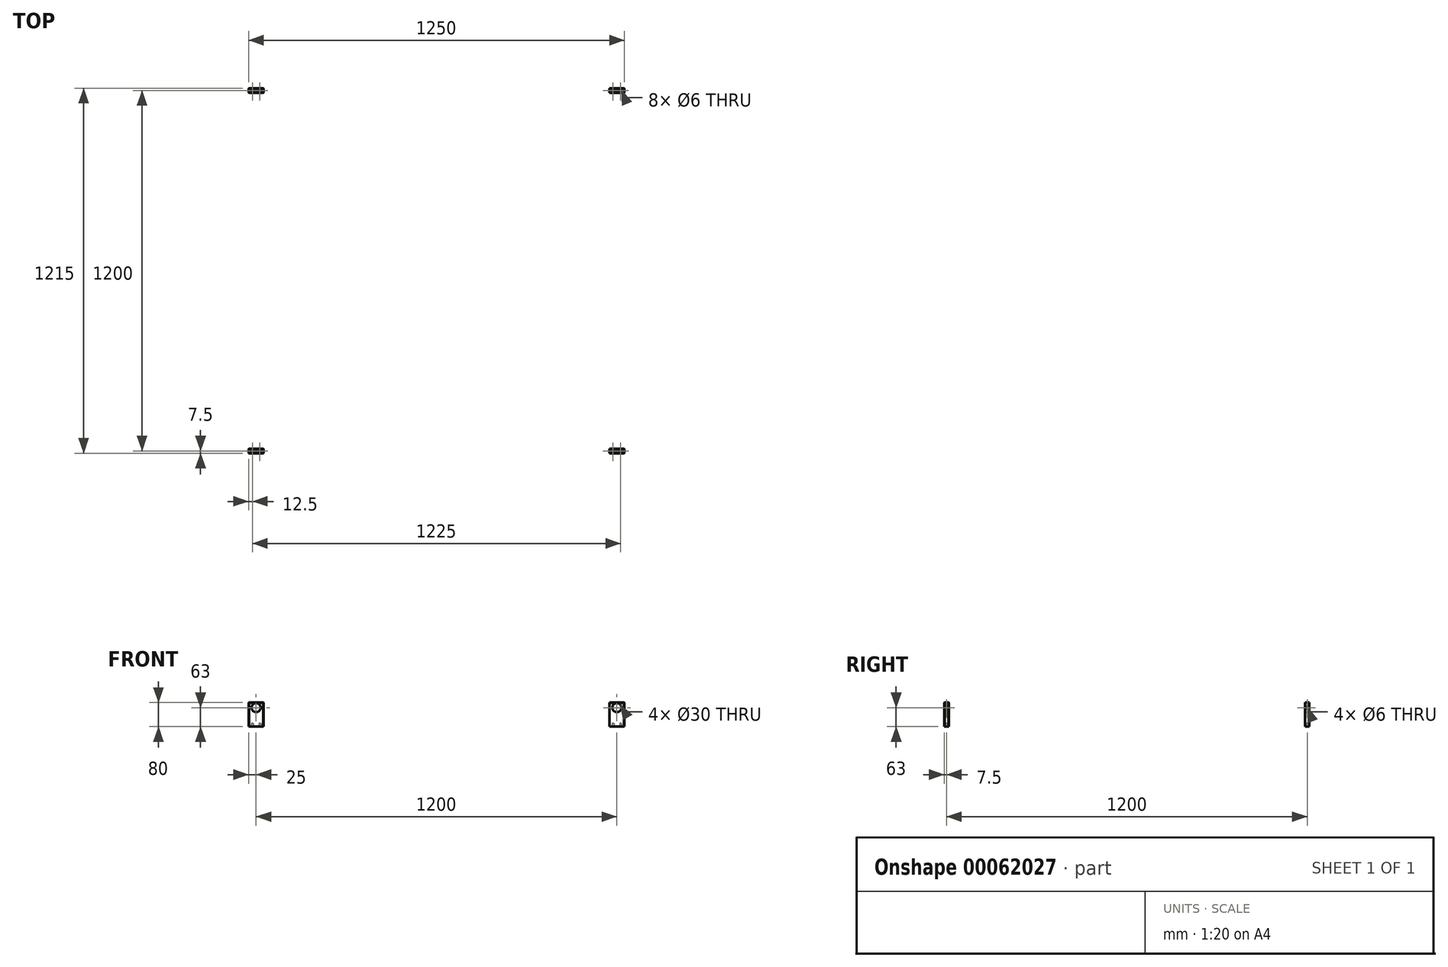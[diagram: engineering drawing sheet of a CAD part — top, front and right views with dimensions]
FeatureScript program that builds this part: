
annotation { "Feature Type Name" : "Feature", "Feature Type Description" : "" }
export const myFeature = defineFeature(function(context is Context, id is Id, definition is map)
    precondition{}
    {
        {
            var Q0;
            Q0=qCreatedBy(makeId("Front.planeOp"),FACE);
            var sketch = newSketch(context, id + "F0", { "sketchPlane" : qUnion([Q0])});
            skCircle(sketch, "E0", {"center": v(0, 0) * mm, "radius": 15 * mm});
            skLineSegment(sketch, "E1.bottom", {"start": v(-25, 17) * mm, "end": v(25, 17) * mm});
            skLineSegment(sketch, "E1.top", {"start": v(-25, -63) * mm, "end": v(25, -63) * mm});
            skLineSegment(sketch, "E1.left", {"start": v(-25, 17) * mm, "end": v(-25, -63) * mm});
            skLineSegment(sketch, "E1.right", {"start": v(25, 17) * mm, "end": v(25, -63) * mm});
            skSolve(sketch);
        }
        {
            var Q0;
            Q0=makeQuery(id+"F0.imprint","IMPRINT",FACE,{"disambiguationData":[TD([[makeQuery(id+"F0.imprint","IMPRINT",EDGE,{"derivedFrom":sQuery(id+"F0.wireOp",EDGE,"E0")}),-1.0]])]});
            extrude(context, id + "F1", {"entities" : qUnion([Q0]), "depth" : 15 * mm});
        }
        {
            var Q0;
            Q0=makeQuery(id+"F1.opExtrude","SWEPT_FACE",FACE,{"disambiguationData":[OSD([sQuery(id+"F0.wireOp",EDGE,"E1.top")])]});
            var sketch = newSketch(context, id + "F2", { "sketchPlane" : qUnion([Q0])});
            skCircle(sketch, "E2", {"center": v(12.5, 7.5) * mm, "radius": 3 * mm});
            skCircle(sketch, "E3.MirrorC", {"center": v(-12.5, 7.5) * mm, "radius": 3 * mm});
            skSolve(sketch);
        }
        {
            var Q0;
            Q0=sQuery(id+"F2.wireOp",VERTEX,"E2.center");
            var Q1;
            Q1=sQuery(id+"F2.wireOp",VERTEX,"E3.MirrorC.center");
            var Q2;
            Q2=makeQuery(id+"F1.opExtrude","SWEPT_BODY",BODY,{"disambiguationData":[OSD([sQuery(id+"F0.wireOp",EDGE,"E0"),sQuery(id+"F0.wireOp",EDGE,"E1.bottom"),sQuery(id+"F0.wireOp",EDGE,"E1.top"),sQuery(id+"F0.wireOp",EDGE,"E1.left"),sQuery(id+"F0.wireOp",EDGE,"E1.right")])]});
            hole(context, id + "F3", {"style" : HoleStyle.SIMPLE, "holeDiameter" : 6 * mm, "endStyle" : HoleEndStyle.BLIND, "holeDepth" : 10 * mm, "locations" : qUnion([Q0, Q1]), "scope" : qUnion([Q2])});
        }
        {
            var Q0;
            Q0=makeQuery(id+"F1.opExtrude","SWEPT_FACE",FACE,{"disambiguationData":[OSD([sQuery(id+"F0.wireOp",EDGE,"E1.right")])]});
            var sketch = newSketch(context, id + "F4", { "sketchPlane" : qUnion([Q0])});
            skCircle(sketch, "E4", {"center": v(-7.5, 0) * mm, "radius": 3 * mm});
            skSolve(sketch);
        }
        {
            var Q0;
            Q0=sQuery(id+"F4.wireOp",VERTEX,"E4.center");
            var Q1;
            Q1=makeQuery(id+"F1.opExtrude","SWEPT_BODY",BODY,{"disambiguationData":[OSD([sQuery(id+"F0.wireOp",EDGE,"E0"),sQuery(id+"F0.wireOp",EDGE,"E1.bottom"),sQuery(id+"F0.wireOp",EDGE,"E1.top"),sQuery(id+"F0.wireOp",EDGE,"E1.left"),sQuery(id+"F0.wireOp",EDGE,"E1.right")])]});
            hole(context, id + "F5", {"style" : HoleStyle.SIMPLE, "holeDiameter" : 6 * mm, "endStyle" : HoleEndStyle.BLIND, "holeDepth" : 20 * mm, "locations" : qUnion([Q0]), "scope" : qUnion([Q1])});
        }
        {
            var Q0;
            Q0=makeQuery(id+"F1.opExtrude","CAP_EDGE",EDGE,{"disambiguationData":[OSD([sQuery(id+"F0.wireOp",EDGE,"E1.bottom")])],"isStart":false});
            var Q1;
            Q1=makeQuery(id+"F1.opExtrude","CAP_EDGE",EDGE,{"disambiguationData":[OSD([sQuery(id+"F0.wireOp",EDGE,"E1.bottom")])],"isStart":true});
            var Q2;
            Q2=makeQuery(id+"F1.opExtrude","SWEPT_EDGE",EDGE,{"disambiguationData":[OSD([sQuery(id+"F0.wireOp",EDGE,"E1.bottom"),sQuery(id+"F0.wireOp",EDGE,"E1.right")])]});
            var Q3;
            Q3=makeQuery(id+"F1.opExtrude","SWEPT_EDGE",EDGE,{"disambiguationData":[OSD([sQuery(id+"F0.wireOp",EDGE,"E1.bottom"),sQuery(id+"F0.wireOp",EDGE,"E1.left")])]});
            var Q4;
            Q4=makeQuery(id+"F1.opExtrude","CAP_EDGE",EDGE,{"disambiguationData":[OSD([sQuery(id+"F0.wireOp",EDGE,"E1.right")])],"isStart":false});
            var Q5;
            Q5=makeQuery(id+"F1.opExtrude","CAP_EDGE",EDGE,{"disambiguationData":[OSD([sQuery(id+"F0.wireOp",EDGE,"E1.right")])],"isStart":true});
            var Q6;
            Q6=makeQuery(id+"F1.opExtrude","CAP_EDGE",EDGE,{"disambiguationData":[OSD([sQuery(id+"F0.wireOp",EDGE,"E1.left")])],"isStart":false});
            var Q7;
            Q7=makeQuery(id+"F1.opExtrude","CAP_EDGE",EDGE,{"disambiguationData":[OSD([sQuery(id+"F0.wireOp",EDGE,"E1.left")])],"isStart":true});
            chamfer(context, id + "F6", {"entities" : qUnion([Q0, Q1, Q2, Q3, Q4, Q5, Q6, Q7]), "width" : 1 * mm, "tangentPropagation" : true});
        }
        {
            var Q0;
            Q0=makeQuery(id+"F1.opExtrude","SWEPT_BODY",BODY,{"disambiguationData":[OSD([sQuery(id+"F0.wireOp",EDGE,"E0"),sQuery(id+"F0.wireOp",EDGE,"E1.bottom"),sQuery(id+"F0.wireOp",EDGE,"E1.top"),sQuery(id+"F0.wireOp",EDGE,"E1.left"),sQuery(id+"F0.wireOp",EDGE,"E1.right")])]});
            transform(context, id + "F7", {"entities" : qUnion([Q0]), "transformType" : TransformType.TRANSLATION_3D, "dx" : 0 * mm, "dy" : 1200 * mm, "dz" : 0 * mm, "makeCopy" : true});
        }
        {
            var Q0;
            Q0=makeQuery(id+"F1.opExtrude","SWEPT_BODY",BODY,{"disambiguationData":[OSD([sQuery(id+"F0.wireOp",EDGE,"E0"),sQuery(id+"F0.wireOp",EDGE,"E1.bottom"),sQuery(id+"F0.wireOp",EDGE,"E1.top"),sQuery(id+"F0.wireOp",EDGE,"E1.left"),sQuery(id+"F0.wireOp",EDGE,"E1.right")])]});
            transform(context, id + "F8", {"entities" : qUnion([Q0]), "transformType" : TransformType.TRANSLATION_3D, "dx" : 1200 * mm, "dy" : 0 * mm, "dz" : 0 * mm, "makeCopy" : true});
        }
        {
            var Q0;
            Q0=makeQuery(id+"F7.opPattern","COPY",BODY,{"derivedFrom":makeQuery(id+"F1.opExtrude","SWEPT_BODY",BODY,{"disambiguationData":[OSD([sQuery(id+"F0.wireOp",EDGE,"E0"),sQuery(id+"F0.wireOp",EDGE,"E1.bottom"),sQuery(id+"F0.wireOp",EDGE,"E1.top"),sQuery(id+"F0.wireOp",EDGE,"E1.left"),sQuery(id+"F0.wireOp",EDGE,"E1.right")])]}),"instanceName":"1"});
            var Q1;
            Q1=makeQuery(id+"F8.opPattern","COPY",BODY,{"derivedFrom":makeQuery(id+"F1.opExtrude","SWEPT_BODY",BODY,{"disambiguationData":[OSD([sQuery(id+"F0.wireOp",EDGE,"E0"),sQuery(id+"F0.wireOp",EDGE,"E1.bottom"),sQuery(id+"F0.wireOp",EDGE,"E1.top"),sQuery(id+"F0.wireOp",EDGE,"E1.left"),sQuery(id+"F0.wireOp",EDGE,"E1.right")])]}),"instanceName":"1"});
            transform(context, id + "F9", {"entities" : qUnion([Q0, Q1]), "transformType" : TransformType.TRANSLATION_3D, "dx" : 1200 * mm, "dy" : 0 * mm, "dz" : 0 * mm, "makeCopy" : true});
        }
        {
            var Q0;
            Q0=makeQuery(id+"F9.opPattern","COPY",BODY,{"derivedFrom":makeQuery(id+"F8.opPattern","COPY",BODY,{"derivedFrom":makeQuery(id+"F1.opExtrude","SWEPT_BODY",BODY,{"disambiguationData":[OSD([sQuery(id+"F0.wireOp",EDGE,"E0"),sQuery(id+"F0.wireOp",EDGE,"E1.bottom"),sQuery(id+"F0.wireOp",EDGE,"E1.top"),sQuery(id+"F0.wireOp",EDGE,"E1.left"),sQuery(id+"F0.wireOp",EDGE,"E1.right")])]}),"instanceName":"1"}),"instanceName":"1"});
            deleteBodies(context, id + "F10", {"entities" : qUnion([Q0])});
        }
    });
